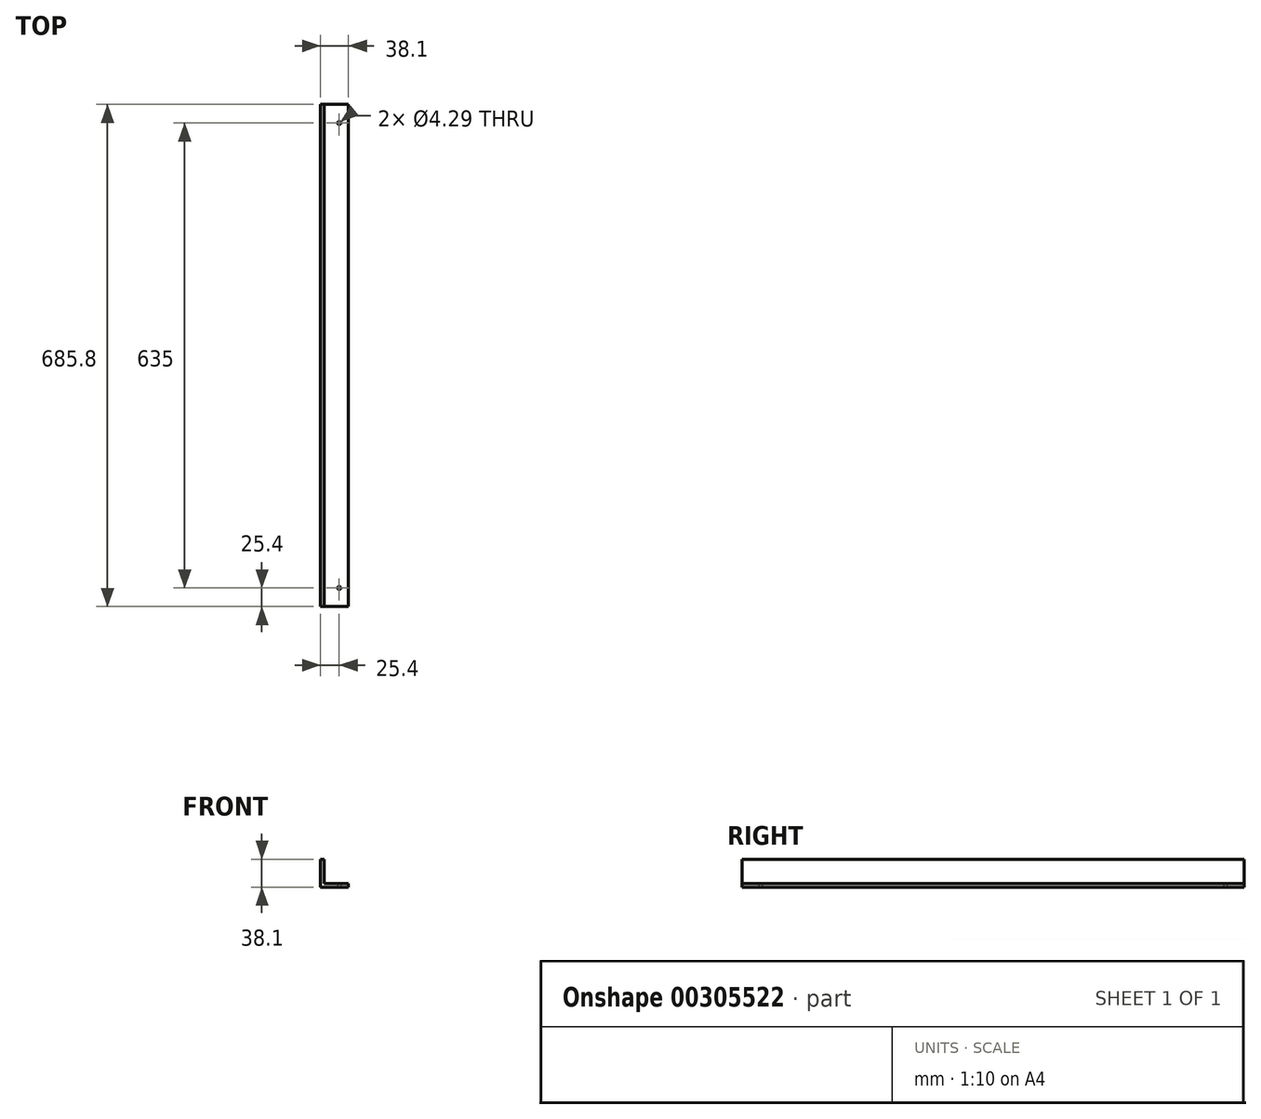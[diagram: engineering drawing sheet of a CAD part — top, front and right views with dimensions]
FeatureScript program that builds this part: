
annotation { "Feature Type Name" : "Feature", "Feature Type Description" : "" }
export const myFeature = defineFeature(function(context is Context, id is Id, definition is map)
    precondition{}
    {
        {
            var Q0;
            Q0=qCreatedBy(makeId("Front.planeOp"),FACE);
            var sketch = newSketch(context, id + "F0", { "sketchPlane" : qUnion([Q0])});
            skLineSegment(sketch, "E0.bottom", {"start": v(0, 0) * mm, "end": v(38.1, 0) * mm});
            skLineSegment(sketch, "E0.top", {"start": v(0, 38.1) * mm, "end": v(4.76, 38.1) * mm});
            skLineSegment(sketch, "E0.left", {"start": v(0, 0) * mm, "end": v(0, 38.1) * mm});
            skLineSegment(sketch, "E0.right", {"start": v(38.1, 0) * mm, "end": v(38.1, 4.76) * mm});
            skLineSegment(sketch, "E1.top", {"start": v(38.1, 4.76) * mm, "end": v(4.76, 4.76) * mm});
            skLineSegment(sketch, "E1.right", {"start": v(4.76, 38.1) * mm, "end": v(4.76, 4.76) * mm});
            skSolve(sketch);
        }
        {
            var Q0;
            Q0 = qSketchRegion(id + "F0", true);
            extrude(context, id + "F1", {"entities" : qUnion([Q0]), "depth" : 685.8 * mm});
        }
        {
            var Q0;
            Q0=makeQuery(id+"F1.opExtrude","SWEPT_FACE",FACE,{"disambiguationData":[OSD([sQuery(id+"F0.wireOp",EDGE,"E0.bottom")])]});
            var sketch = newSketch(context, id + "F2", { "sketchPlane" : qUnion([Q0])});
            skCircle(sketch, "E2", {"center": v(25.4, 660.4) * mm, "radius": 2.15 * mm});
            skPoint(sketch, "E2.centerSnap0", {"position": v(19.05, 685.8) * mm});
            skLineSegment(sketch, "E3", {"start": v(38.1, 342.9) * mm, "end": v(0, 342.9) * mm, "construction": true});
            skCircle(sketch, "E4.MirrorC", {"center": v(25.4, 25.4) * mm, "radius": 2.15 * mm});
            skSolve(sketch);
        }
        {
            var Q0;
            Q0 = qSketchRegion(id + "F2", true);
            extrude(context, id + "F3", {"entities" : qUnion([Q0]), "operationType" : NewBodyOperationType.REMOVE, "oppositeDirection" : true, "depth" : 25.4 * mm});
        }
    });
